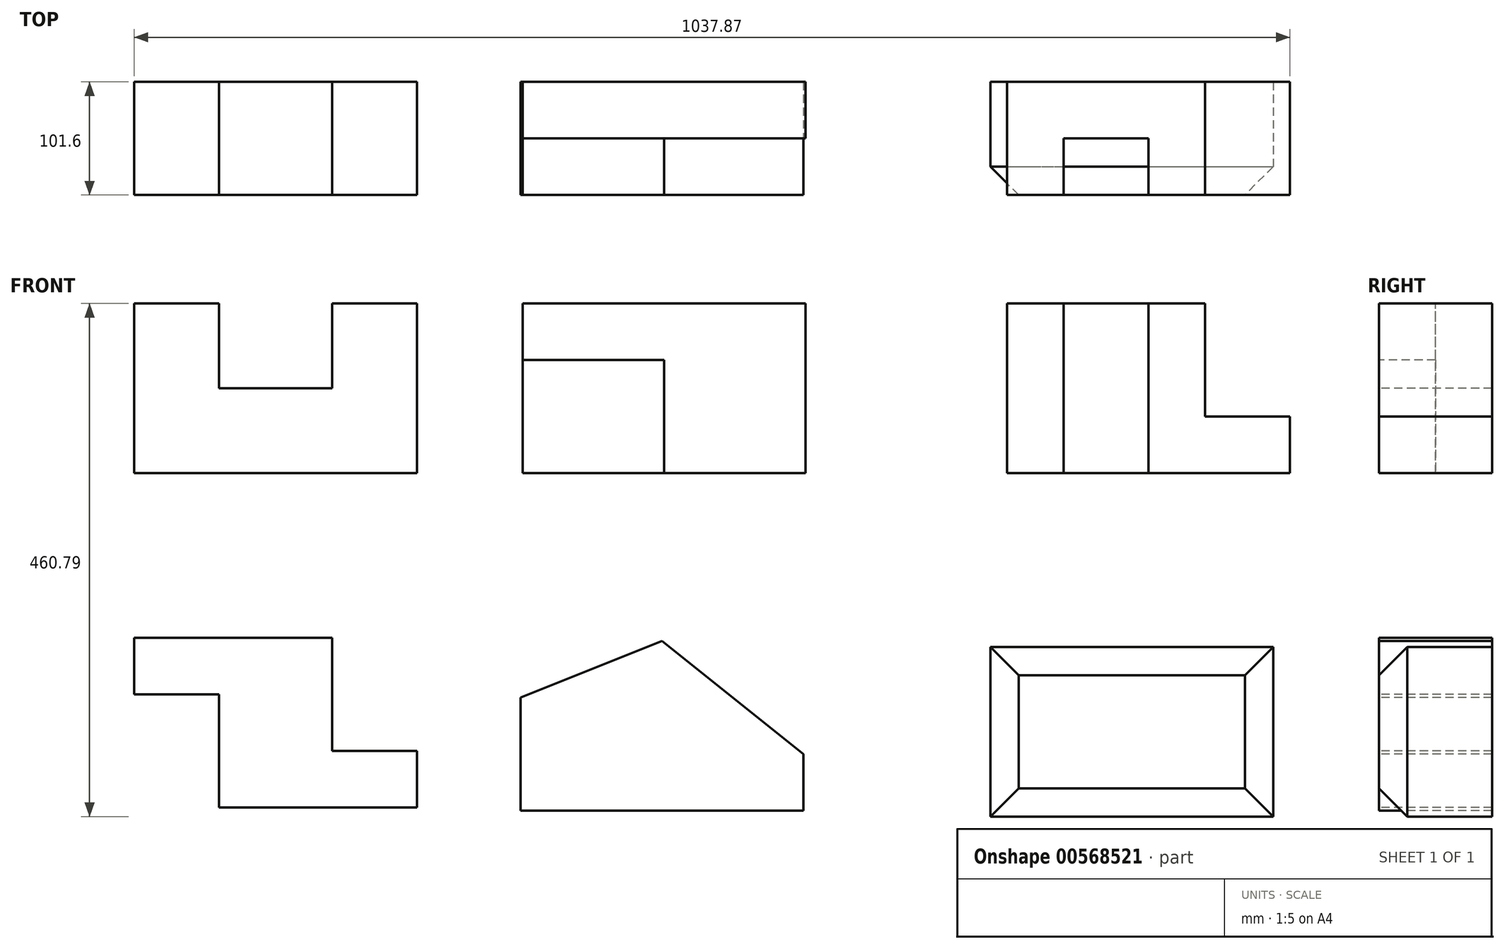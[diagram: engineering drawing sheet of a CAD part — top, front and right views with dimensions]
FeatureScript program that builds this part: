
annotation { "Feature Type Name" : "Feature", "Feature Type Description" : "" }
export const myFeature = defineFeature(function(context is Context, id is Id, definition is map)
    precondition{}
    {
        {
            var Q0;
            Q0=qCreatedBy(makeId("Front.planeOp"),FACE);
            var sketch = newSketch(context, id + "F0", { "sketchPlane" : qUnion([Q0])});
            skLineSegment(sketch, "E0", {"start": v(0, 0) * mm, "end": v(254, 0) * mm});
            skLineSegment(sketch, "E1", {"start": v(254, 0) * mm, "end": v(254, 152.4) * mm});
            skLineSegment(sketch, "E2", {"start": v(254, 152.4) * mm, "end": v(177.8, 152.4) * mm});
            skLineSegment(sketch, "E3", {"start": v(177.8, 152.4) * mm, "end": v(177.8, 76.2) * mm});
            skLineSegment(sketch, "E4", {"start": v(177.8, 76.2) * mm, "end": v(76.2, 76.2) * mm});
            skLineSegment(sketch, "E5", {"start": v(76.2, 76.2) * mm, "end": v(76.2, 152.4) * mm});
            skLineSegment(sketch, "E6", {"start": v(76.2, 152.4) * mm, "end": v(0, 152.4) * mm});
            skLineSegment(sketch, "E7", {"start": v(0, 152.4) * mm, "end": v(0, 0) * mm});
            skSolve(sketch);
        }
        {
            var Q0;
            Q0=makeQuery(id+"F0.imprint","IMPRINT",FACE,{"disambiguationData":[TD([[makeQuery(id+"F0.imprint","IMPRINT",EDGE,{"derivedFrom":sQuery(id+"F0.wireOp",EDGE,"E0")}),1.0]])]});
            extrude(context, id + "F1", {"entities" : qUnion([Q0]), "oppositeDirection" : true, "depth" : 101.6 * mm, "offsetDistance" : 25.4 * mm});
        }
        {
            var Q0;
            Q0=qCreatedBy(makeId("Front.planeOp"),FACE);
            var sketch = newSketch(context, id + "F2", { "sketchPlane" : qUnion([Q0])});
            skLineSegment(sketch, "E8.bottom", {"start": v(349.02, 0) * mm, "end": v(603.02, 0) * mm});
            skLineSegment(sketch, "E8.top", {"start": v(349.02, 152.4) * mm, "end": v(603.02, 152.4) * mm});
            skLineSegment(sketch, "E8.left", {"start": v(349.02, 0) * mm, "end": v(349.02, 152.4) * mm});
            skLineSegment(sketch, "E8.right", {"start": v(603.02, 0) * mm, "end": v(603.02, 152.4) * mm});
            skSolve(sketch);
        }
        {
            var Q0;
            Q0=makeQuery(id+"F2.imprint","IMPRINT",FACE,{"disambiguationData":[TD([[makeQuery(id+"F2.imprint","IMPRINT",EDGE,{"derivedFrom":sQuery(id+"F2.wireOp",EDGE,"E8.bottom")}),1.0]])]});
            extrude(context, id + "F3", {"entities" : qUnion([Q0]), "oppositeDirection" : true, "depth" : 101.6 * mm, "offsetDistance" : 25.4 * mm});
        }
        {
            var Q0;
            Q0=makeQuery(id+"F3.opExtrude","CAP_FACE",FACE,{"disambiguationData":[OSD([sQuery(id+"F2.wireOp",EDGE,"E8.bottom"),sQuery(id+"F2.wireOp",EDGE,"E8.top"),sQuery(id+"F2.wireOp",EDGE,"E8.left"),sQuery(id+"F2.wireOp",EDGE,"E8.right")])],"isStart":true});
            var sketch = newSketch(context, id + "F4", { "sketchPlane" : qUnion([Q0])});
            skLineSegment(sketch, "E9", {"start": v(349.02, 152.4) * mm, "end": v(349.02, 101.6) * mm});
            skLineSegment(sketch, "E10", {"start": v(349.02, 101.6) * mm, "end": v(476.02, 101.6) * mm});
            skLineSegment(sketch, "E11", {"start": v(476.02, 101.6) * mm, "end": v(476.02, 0) * mm});
            skLineSegment(sketch, "E12", {"start": v(476.02, 0) * mm, "end": v(603.02, 0) * mm});
            skLineSegment(sketch, "E13", {"start": v(603.02, 0) * mm, "end": v(603.02, 152.4) * mm});
            skLineSegment(sketch, "E14", {"start": v(603.02, 152.4) * mm, "end": v(349.02, 152.4) * mm});
            skSolve(sketch);
        }
        {
            var Q0;
            Q0=makeQuery(id+"F4.imprint","IMPRINT",FACE,{"disambiguationData":[TD([[makeQuery(id+"F4.imprint","IMPRINT",EDGE,{"derivedFrom":sQuery(id+"F4.wireOp",EDGE,"E9")}),-1.0]])]});
            extrude(context, id + "F5", {"entities" : qUnion([Q0]), "operationType" : NewBodyOperationType.REMOVE, "oppositeDirection" : true, "depth" : 50.8 * mm, "offsetDistance" : 25.4 * mm});
        }
        {
            var Q0;
            Q0=qCreatedBy(makeId("Front.planeOp"),FACE);
            var sketch = newSketch(context, id + "F6", { "sketchPlane" : qUnion([Q0])});
            skLineSegment(sketch, "E15.bottom", {"start": v(783.87, 0) * mm, "end": v(1037.87, 0) * mm});
            skLineSegment(sketch, "E15.left", {"start": v(783.87, 0) * mm, "end": v(783.87, 152.4) * mm});
            skPoint(sketch, "E16", {"position": v(834.67, 152.4) * mm});
            skPoint(sketch, "E17", {"position": v(910.87, 152.4) * mm});
            skPoint(sketch, "E18", {"position": v(961.67, 152.4) * mm});
            skLineSegment(sketch, "E19", {"start": v(834.67, 152.4) * mm, "end": v(834.67, 0) * mm});
            skLineSegment(sketch, "E20", {"start": v(910.87, 152.4) * mm, "end": v(910.87, 0) * mm});
            skLineSegment(sketch, "E21", {"start": v(961.67, 152.4) * mm, "end": v(961.67, 50.8) * mm});
            skLineSegment(sketch, "E22", {"start": v(961.67, 50.8) * mm, "end": v(1037.87, 50.8) * mm});
            skLineSegment(sketch, "E23", {"start": v(783.87, 152.4) * mm, "end": v(961.67, 152.4) * mm});
            skLineSegment(sketch, "E24", {"start": v(1037.87, 50.8) * mm, "end": v(1037.87, 0) * mm});
            skSolve(sketch);
        }
        {
            var Q0;
            {var subQ0=sQuery(id+"F6.wireOp",EDGE,"E15.left");Q0=makeQuery(id+"F6.imprint","IMPRINT",FACE,{"disambiguationData":[TD([[makeQuery(id+"F6.imprint","IMPRINT",EDGE,{"derivedFrom":subQ0}),-1.0]])]});}
            var Q1;
            {var subQ1=sQuery(id+"F6.wireOp",EDGE,"E20");Q1=makeQuery(id+"F6.imprint","IMPRINT",FACE,{"disambiguationData":[TD([[makeQuery(id+"F6.imprint","IMPRINT",EDGE,{"derivedFrom":subQ1}),1.0]])]});}
            var Q2;
            {var subQ0=sQuery(id+"F6.wireOp",EDGE,"E19");Q2=makeQuery(id+"F6.imprint","IMPRINT",FACE,{"disambiguationData":[TD([[makeQuery(id+"F6.imprint","IMPRINT",EDGE,{"derivedFrom":subQ0}),1.0]])]});}
            extrude(context, id + "F7", {"entities" : qUnion([Q0, Q1, Q2]), "oppositeDirection" : true, "depth" : 101.6 * mm, "offsetDistance" : 25.4 * mm});
        }
        {
            var Q0;
            Q0=makeQuery(id+"F7.opExtrude","CAP_FACE",FACE,{"disambiguationData":[OSD([sQuery(id+"F6.wireOp",EDGE,"E15.bottom"),sQuery(id+"F6.wireOp",EDGE,"E15.left"),sQuery(id+"F6.wireOp",EDGE,"E21"),sQuery(id+"F6.wireOp",EDGE,"E22"),sQuery(id+"F6.wireOp",EDGE,"E23"),sQuery(id+"F6.wireOp",EDGE,"E24")])],"isStart":true});
            var sketch = newSketch(context, id + "F8", { "sketchPlane" : qUnion([Q0])});
            skLineSegment(sketch, "E25", {"start": v(834.67, 152.4) * mm, "end": v(834.67, 0) * mm});
            skLineSegment(sketch, "E26", {"start": v(834.67, 0) * mm, "end": v(783.87, 0) * mm});
            skLineSegment(sketch, "E27", {"start": v(783.87, 0) * mm, "end": v(783.87, 152.4) * mm});
            skLineSegment(sketch, "E28", {"start": v(783.87, 152.4) * mm, "end": v(834.67, 152.4) * mm});
            skLineSegment(sketch, "E29", {"start": v(834.67, 152.4) * mm, "end": v(910.87, 152.4) * mm});
            skLineSegment(sketch, "E30", {"start": v(910.87, 152.4) * mm, "end": v(910.87, 0) * mm});
            skLineSegment(sketch, "E31", {"start": v(910.87, 0) * mm, "end": v(834.67, 0) * mm});
            skSolve(sketch);
        }
        {
            var Q0;
            Q0=makeQuery(id+"F8.imprint","IMPRINT",FACE,{"disambiguationData":[TD([[makeQuery(id+"F8.imprint","IMPRINT",EDGE,{"derivedFrom":sQuery(id+"F8.wireOp",EDGE,"E25")}),1.0]])]});
            extrude(context, id + "F9", {"entities" : qUnion([Q0]), "operationType" : NewBodyOperationType.REMOVE, "oppositeDirection" : true, "depth" : 50.8 * mm, "offsetDistance" : 25.4 * mm});
        }
        {
            var Q0;
            Q0=qCreatedBy(makeId("Front.planeOp"),FACE);
            var sketch = newSketch(context, id + "F10", { "sketchPlane" : qUnion([Q0])});
            skLineSegment(sketch, "E32.bottom", {"start": v(0, -147.96) * mm, "end": v(177.8, -147.96) * mm});
            skLineSegment(sketch, "E32.top", {"start": v(76.2, -300.36) * mm, "end": v(254, -300.36) * mm});
            skLineSegment(sketch, "E32.left", {"start": v(0, -147.96) * mm, "end": v(0, -198.76) * mm});
            skLineSegment(sketch, "E32.right", {"start": v(254, -249.56) * mm, "end": v(254, -300.36) * mm});
            skPoint(sketch, "E33", {"position": v(0, -198.76) * mm});
            skPoint(sketch, "E34", {"position": v(254, -249.56) * mm});
            skLineSegment(sketch, "E35", {"start": v(0, -198.76) * mm, "end": v(76.2, -198.76) * mm});
            skLineSegment(sketch, "E36", {"start": v(76.2, -198.76) * mm, "end": v(76.2, -300.36) * mm});
            skLineSegment(sketch, "E37", {"start": v(254, -249.56) * mm, "end": v(177.8, -249.56) * mm});
            skLineSegment(sketch, "E38", {"start": v(177.8, -249.56) * mm, "end": v(177.8, -147.96) * mm});
            skSolve(sketch);
        }
        {
            var Q0;
            Q0=makeQuery(id+"F10.imprint","IMPRINT",FACE,{"disambiguationData":[TD([[makeQuery(id+"F10.imprint","IMPRINT",EDGE,{"derivedFrom":sQuery(id+"F10.wireOp",EDGE,"E32.bottom")}),-1.0]])]});
            extrude(context, id + "F11", {"entities" : qUnion([Q0]), "oppositeDirection" : true, "depth" : 101.6 * mm, "offsetDistance" : 25.4 * mm});
        }
        {
            var Q0;
            Q0=qCreatedBy(makeId("Front.planeOp"),FACE);
            var sketch = newSketch(context, id + "F12", { "sketchPlane" : qUnion([Q0])});
            skPoint(sketch, "E39", {"position": v(346.94, -302.98) * mm});
            skLineSegment(sketch, "E40.bottom", {"start": v(346.94, -302.98) * mm, "end": v(600.94, -302.98) * mm});
            skLineSegment(sketch, "E40.left", {"start": v(346.94, -302.98) * mm, "end": v(346.94, -201.38) * mm});
            skLineSegment(sketch, "E40.right", {"start": v(600.94, -302.98) * mm, "end": v(600.94, -252.18) * mm});
            skPoint(sketch, "E41", {"position": v(473.94, -150.58) * mm});
            skPoint(sketch, "E42", {"position": v(600.94, -252.18) * mm});
            skPoint(sketch, "E43", {"position": v(346.94, -201.38) * mm});
            skLineSegment(sketch, "E44", {"start": v(346.94, -201.38) * mm, "end": v(473.94, -150.58) * mm});
            skLineSegment(sketch, "E45", {"start": v(473.94, -150.58) * mm, "end": v(600.94, -252.18) * mm});
            skSolve(sketch);
        }
        {
            var Q0;
            Q0=makeQuery(id+"F12.imprint","IMPRINT",FACE,{"disambiguationData":[TD([[makeQuery(id+"F12.imprint","IMPRINT",EDGE,{"derivedFrom":sQuery(id+"F12.wireOp",EDGE,"E40.bottom")}),1.0]])]});
            extrude(context, id + "F13", {"entities" : qUnion([Q0]), "oppositeDirection" : true, "depth" : 101.6 * mm, "offsetDistance" : 25.4 * mm});
        }
        {
            var Q0;
            Q0=qCreatedBy(makeId("Front.planeOp"),FACE);
            var sketch = newSketch(context, id + "F14", { "sketchPlane" : qUnion([Q0])});
            skPoint(sketch, "E46", {"position": v(768.86, -308.39) * mm});
            skLineSegment(sketch, "E47.bottom", {"start": v(768.86, -308.39) * mm, "end": v(1022.86, -308.39) * mm});
            skLineSegment(sketch, "E47.top", {"start": v(768.86, -155.99) * mm, "end": v(1022.86, -155.99) * mm});
            skLineSegment(sketch, "E47.left", {"start": v(768.86, -308.39) * mm, "end": v(768.86, -155.99) * mm});
            skLineSegment(sketch, "E47.right", {"start": v(1022.86, -308.39) * mm, "end": v(1022.86, -155.99) * mm});
            skSolve(sketch);
        }
        {
            var Q0;
            Q0=makeQuery(id+"F14.imprint","IMPRINT",FACE,{"disambiguationData":[TD([[makeQuery(id+"F14.imprint","IMPRINT",EDGE,{"derivedFrom":sQuery(id+"F14.wireOp",EDGE,"E47.bottom")}),1.0]])]});
            extrude(context, id + "F15", {"entities" : qUnion([Q0]), "operationType" : NewBodyOperationType.ADD, "oppositeDirection" : true, "depth" : 101.6 * mm, "offsetDistance" : 25.4 * mm});
        }
        {
            var Q0;
            Q0=makeQuery(id+"F15.opExtrude","SWEPT_FACE",FACE,{"disambiguationData":[OSD([sQuery(id+"F14.wireOp",EDGE,"E47.right")])]});
            var sketch = newSketch(context, id + "F16", { "sketchPlane" : qUnion([Q0])});
            skLineSegment(sketch, "E48", {"start": v(25.4, -155.99) * mm, "end": v(0, -181.39) * mm});
            skLineSegment(sketch, "E49", {"start": v(0, -282.99) * mm, "end": v(25.4, -308.39) * mm});
            skSolve(sketch);
        }
        {
            var Q0;
            {var subQ0=sQuery(id+"F16.wireOp",EDGE,"E48");Q0=makeQuery(id+"F16.imprint","IMPRINT",FACE,{"disambiguationData":[TD([[makeQuery(id+"F16.imprint","IMPRINT",EDGE,{"derivedFrom":subQ0}),-1.0]])]});}
            var Q1;
            {var subQ0=sQuery(id+"F16.wireOp",EDGE,"E49");Q1=makeQuery(id+"F16.imprint","IMPRINT",FACE,{"disambiguationData":[TD([[makeQuery(id+"F16.imprint","IMPRINT",EDGE,{"derivedFrom":subQ0}),-1.0]])]});}
            extrude(context, id + "F17", {"entities" : qUnion([Q0, Q1]), "operationType" : NewBodyOperationType.REMOVE, "oppositeDirection" : true, "depth" : 254 * mm, "offsetDistance" : 25.4 * mm});
        }
        {
            var Q0;
            Q0=makeQuery(id+"F15.opExtrude","SWEPT_FACE",FACE,{"disambiguationData":[OSD([sQuery(id+"F14.wireOp",EDGE,"E47.top")])]});
            var sketch = newSketch(context, id + "F18", { "sketchPlane" : qUnion([Q0])});
            skLineSegment(sketch, "E50", {"start": v(794.26, 25.4) * mm, "end": v(768.86, 25.4) * mm});
            skLineSegment(sketch, "E51", {"start": v(997.46, 25.4) * mm, "end": v(1022.86, 25.4) * mm});
            skLineSegment(sketch, "E52", {"start": v(997.46, 0) * mm, "end": v(1022.86, 25.4) * mm});
            skLineSegment(sketch, "E53", {"start": v(794.26, 0) * mm, "end": v(768.86, 25.4) * mm});
            skLineSegment(sketch, "E54", {"start": v(794.26, 25.4) * mm, "end": v(794.26, 0) * mm});
            skLineSegment(sketch, "E55", {"start": v(997.46, 25.4) * mm, "end": v(997.46, 0) * mm});
            skLineSegment(sketch, "E56.MirrorCS", {"start": v(1022.86, 0) * mm, "end": v(1022.86, 25.4) * mm});
            skLineSegment(sketch, "E57.MirrorCS", {"start": v(1022.86, 0) * mm, "end": v(997.46, 0) * mm});
            skLineSegment(sketch, "E58.MirrorCS", {"start": v(768.86, 0) * mm, "end": v(768.86, 25.4) * mm});
            skLineSegment(sketch, "E59.MirrorCS", {"start": v(768.86, 0) * mm, "end": v(794.26, 0) * mm});
            skSolve(sketch);
        }
        {
            var Q0;
            Q0=makeQuery(id+"F18.imprint","IMPRINT",FACE,{"disambiguationData":[TD([[makeQuery(id+"F18.imprint","IMPRINT",EDGE,{"derivedFrom":sQuery(id+"F18.wireOp",EDGE,"E53")}),1.0]])]});
            var Q1;
            Q1=makeQuery(id+"F18.imprint","IMPRINT",FACE,{"disambiguationData":[TD([[makeQuery(id+"F18.imprint","IMPRINT",EDGE,{"derivedFrom":sQuery(id+"F18.wireOp",EDGE,"E52")}),-1.0]])]});
            extrude(context, id + "F19", {"entities" : qUnion([Q0, Q1]), "operationType" : NewBodyOperationType.REMOVE, "oppositeDirection" : true, "depth" : 152.4 * mm, "offsetDistance" : 25.4 * mm});
        }
    });
